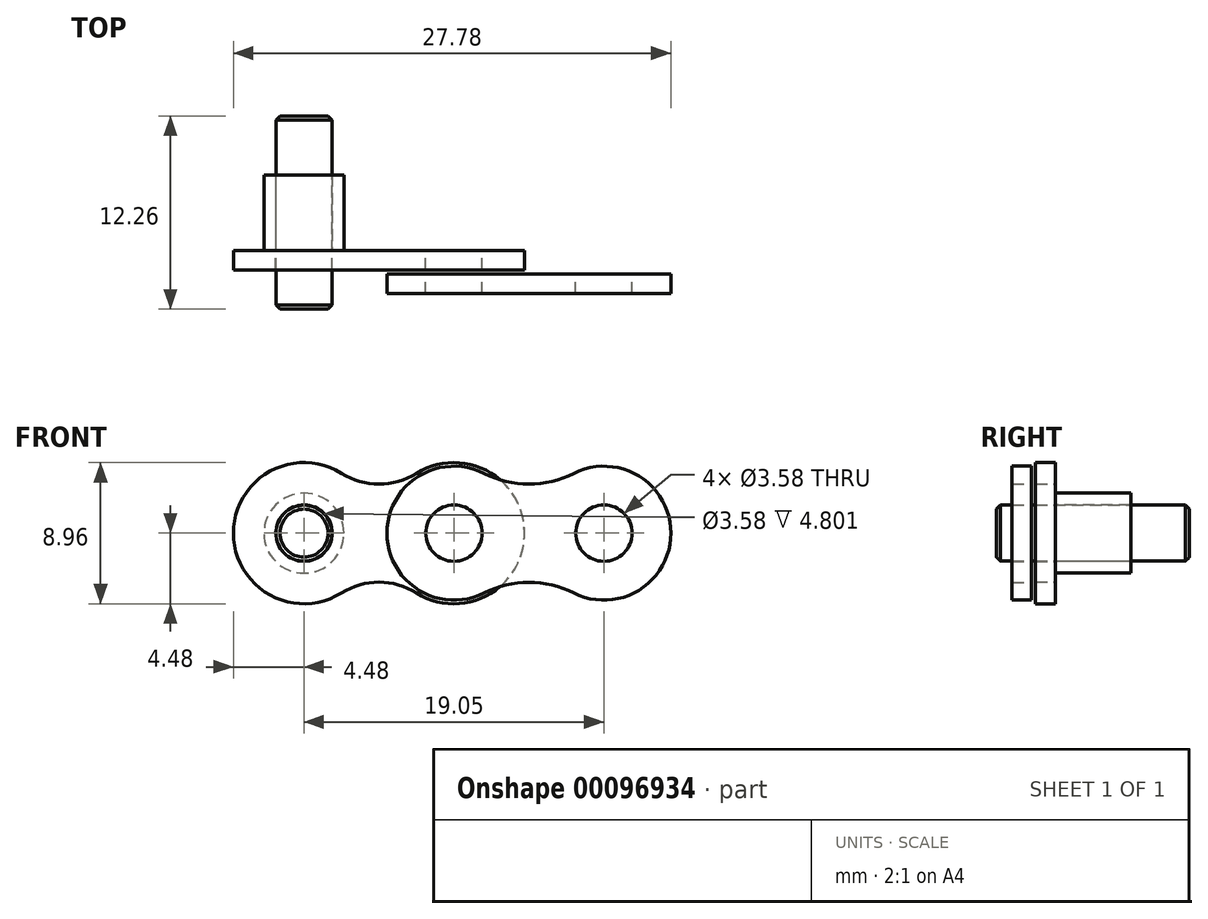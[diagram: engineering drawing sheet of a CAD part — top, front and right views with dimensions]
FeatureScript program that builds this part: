
annotation { "Feature Type Name" : "Feature", "Feature Type Description" : "" }
export const myFeature = defineFeature(function(context is Context, id is Id, definition is map)
    precondition{}
    {
        {
            var Q0;
            Q0=qCreatedBy(makeId("Front.planeOp"),FACE);
            var sketch = newSketch(context, id + "F0", { "sketchPlane" : qUnion([Q0])});
            skArc(sketch, "E0", {"start": v(2.38, 3.8) * mm, "mid": v(-4.48, 0) * mm, "end": v(2.38, -3.8) * mm});
            skArc(sketch, "E1", {"start": v(7.14, -3.8) * mm, "mid": v(14, 0) * mm, "end": v(7.14, 3.8) * mm});
            skLineSegment(sketch, "E2", {"start": v(0, 0) * mm, "end": v(9.53, 0) * mm, "construction": true});
            skLineSegment(sketch, "E3", {"start": v(4.76, 0) * mm, "end": v(4.76, 11.34) * mm, "construction": true});
            skArc(sketch, "E4", {"start": v(2.38, 3.8) * mm, "mid": v(4.76, 3.11) * mm, "end": v(7.14, 3.8) * mm});
            skArc(sketch, "E5.MirrorC", {"start": v(2.38, -3.8) * mm, "mid": v(4.76, -3.11) * mm, "end": v(7.14, -3.8) * mm});
            skCircle(sketch, "E6", {"center": v(0, 0) * mm, "radius": 1.8 * mm});
            skCircle(sketch, "E7", {"center": v(9.53, 0) * mm, "radius": 1.8 * mm});
            skSolve(sketch);
        }
        {
            var Q0;
            Q0 = qSketchRegion(id + "F0", true);
            extrude(context, id + "F1", {"entities" : qUnion([Q0]), "depth" : 1.24 * mm});
        }
        {
            var Q0;
            Q0=makeQuery(id+"F1.opExtrude","CAP_FACE",FACE,{"disambiguationData":[OSD([sQuery(id+"F0.wireOp",EDGE,"E0"),sQuery(id+"F0.wireOp",EDGE,"E1"),sQuery(id+"F0.wireOp",EDGE,"E4"),sQuery(id+"F0.wireOp",EDGE,"E5.MirrorC"),sQuery(id+"F0.wireOp",EDGE,"E6"),sQuery(id+"F0.wireOp",EDGE,"E7")])],"isStart":true});
            var sketch = newSketch(context, id + "F2", { "sketchPlane" : qUnion([Q0])});
            skCircle(sketch, "E8.0", {"center": v(0, 0) * mm, "radius": 1.8 * mm});
            skCircle(sketch, "E9", {"center": v(0, 0) * mm, "radius": 2.54 * mm});
            skSolve(sketch);
        }
        {
            var Q0;
            Q0 = qSketchRegion(id + "F2", true);
            extrude(context, id + "F3", {"entities" : qUnion([Q0]), "depth" : 4.8 * mm});
        }
        {
            var Q0;
            Q0=qCreatedBy(makeId("Right.planeOp"),FACE);
            var sketch = newSketch(context, id + "F4", { "sketchPlane" : qUnion([Q0])});
            skLineSegment(sketch, "E10", {"start": v(0, 0) * mm, "end": v(4.8, 0) * mm, "construction": true});
            skPoint(sketch, "E11", {"position": v(2.4, 0) * mm});
            skSolve(sketch);
        }
        {
            var Q0;
            Q0=qCreatedBy(makeId("Front.planeOp"),FACE);
            var Q1;
            Q1=sQuery(id+"F4.wireOp",VERTEX,"E11");
            cPlane(context, id + "F5", {"entities" : qUnion([Q0, Q1]), "cplaneType" : CPlaneType.PLANE_POINT, "offset" : 152.4 * mm, "width" : 152.4 * mm, "height" : 152.4 * mm});
        }
        {
            var Q0;
            Q0=qCreatedBy(id+"F5.planeOp",FACE);
            var sketch = newSketch(context, id + "F6", { "sketchPlane" : qUnion([Q0])});
            skCircle(sketch, "E12", {"center": v(0, 0) * mm, "radius": 1.78 * mm});
            skSolve(sketch);
        }
        {
            var Q0;
            Q0 = qSketchRegion(id + "F6", true);
            extrude(context, id + "F7", {"entities" : qUnion([Q0]), "endBound" : BoundingType.SYMMETRIC, "depth" : 12.27 * mm});
        }
        {
            var Q0;
            Q0=makeQuery(id+"F7.opExtrude","CAP_EDGE",EDGE,{"disambiguationData":[OSD([sQuery(id+"F6.wireOp",EDGE,"E12")])],"isStart":false});
            var Q1;
            Q1=makeQuery(id+"F7.opExtrude","CAP_EDGE",EDGE,{"disambiguationData":[OSD([sQuery(id+"F6.wireOp",EDGE,"E12")])],"isStart":true});
            chamfer(context, id + "F8", {"entities" : qUnion([Q0, Q1]), "width" : 0.25 * mm, "tangentPropagation" : true});
        }
        {
            var Q0;
            Q0=makeQuery(id+"F1.opExtrude","CAP_FACE",FACE,{"disambiguationData":[OSD([sQuery(id+"F0.wireOp",EDGE,"E0"),sQuery(id+"F0.wireOp",EDGE,"E1"),sQuery(id+"F0.wireOp",EDGE,"E4"),sQuery(id+"F0.wireOp",EDGE,"E5.MirrorC"),sQuery(id+"F0.wireOp",EDGE,"E6"),sQuery(id+"F0.wireOp",EDGE,"E7")])],"isStart":false});
            cPlane(context, id + "F9", {"entities" : qUnion([Q0]), "cplaneType" : CPlaneType.OFFSET, "offset" : 0.25 * mm, "width" : 152.4 * mm, "height" : 152.4 * mm});
        }
        {
            var Q0;
            Q0=qCreatedBy(id+"F9.planeOp",FACE);
            var sketch = newSketch(context, id + "F10", { "sketchPlane" : qUnion([Q0])});
            skCircle(sketch, "E13.0", {"center": v(9.53, 0) * mm, "radius": 1.8 * mm});
            skArc(sketch, "E14", {"start": v(11.44, 3.8) * mm, "mid": v(5.27, 0) * mm, "end": v(11.44, -3.8) * mm});
            skCircle(sketch, "E15", {"center": v(19.05, 0) * mm, "radius": 1.8 * mm});
            skArc(sketch, "E16", {"start": v(17.14, -3.8) * mm, "mid": v(23.3, 0) * mm, "end": v(17.14, 3.8) * mm});
            skLineSegment(sketch, "E17", {"start": v(9.53, 0) * mm, "end": v(19.05, 0) * mm, "construction": true});
            skLineSegment(sketch, "E18", {"start": v(14.29, 0) * mm, "end": v(14.29, 10.88) * mm, "construction": true});
            skArc(sketch, "E19", {"start": v(11.44, 3.8) * mm, "mid": v(14.29, 3.12) * mm, "end": v(17.14, 3.8) * mm});
            skArc(sketch, "E20.MirrorC", {"start": v(11.44, -3.8) * mm, "mid": v(14.29, -3.12) * mm, "end": v(17.14, -3.8) * mm});
            skSolve(sketch);
        }
        {
            var Q0;
            Q0 = qSketchRegion(id + "F10", true);
            extrude(context, id + "F11", {"entities" : qUnion([Q0]), "depth" : 1.24 * mm});
        }
    });
